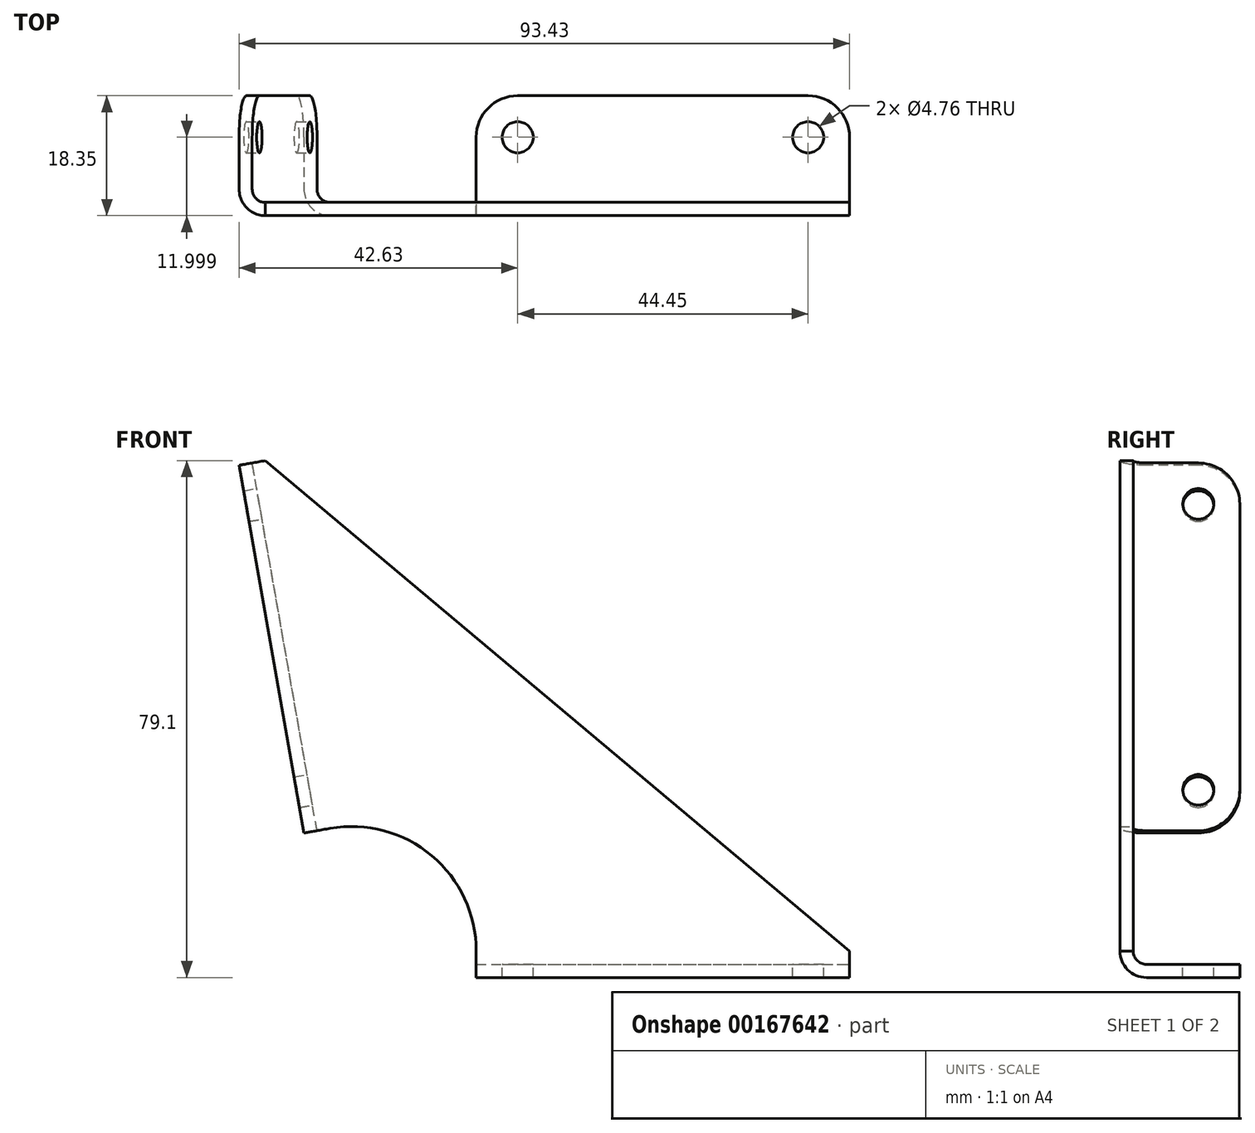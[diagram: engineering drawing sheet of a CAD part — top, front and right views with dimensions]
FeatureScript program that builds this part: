
annotation { "Feature Type Name" : "Feature", "Feature Type Description" : "" }
export const myFeature = defineFeature(function(context is Context, id is Id, definition is map)
    precondition{}
    {
        {
            var Q0;
            Q0=qCreatedBy(makeId("Front.planeOp"),FACE);
            var sketch = newSketch(context, id + "F0", { "sketchPlane" : qUnion([Q0])});
            skLineSegment(sketch, "E0", {"start": v(-3.3, 18.76) * mm, "end": v(-13.23, 75.04) * mm});
            skLineSegment(sketch, "E1", {"start": v(19.05, 0) * mm, "end": v(76.2, 0) * mm});
            skLineSegment(sketch, "E2", {"start": v(-13.23, 75.04) * mm, "end": v(76.2, 0) * mm});
            skArc(sketch, "E3", {"start": v(19.05, 0) * mm, "mid": v(12.25, 14.6) * mm, "end": v(-3.3, 18.76) * mm});
            skSolve(sketch);
        }
        {
            var Q0;
            Q0 = qSketchRegion(id + "F0", true);
            extrude(context, id + "F1", {"entities" : qUnion([Q0]), "depth" : 2.03 * mm});
        }
        {
            var Q0;
            Q0=makeQuery(id+"F1.opExtrude","SWEPT_FACE",FACE,{"disambiguationData":[OSD([sQuery(id+"F0.wireOp",EDGE,"E1")])]});
            var sketch = newSketch(context, id + "F2", { "sketchPlane" : qUnion([Q0])});
            skLineSegment(sketch, "E4", {"start": v(51.4, -2.03) * mm, "end": v(29.22, -2.03) * mm, "construction": true});
            skSolve(sketch);
        }
        {
            var Q0;
            {var subQ0=sQuery(id+"F0.wireOp",EDGE,"E1");Q0=makeQuery(id+"F2.imprint","IMPRINT",FACE,{"disambiguationData":[TD([[makeQuery(id+"F2.imprint","IMPRINT",EDGE,{"derivedFrom":makeQuery(id+"F1.opExtrude","CAP_EDGE",EDGE,{"disambiguationData":[OSD([subQ0])],"isStart":true})}),1.0]])]});}
            var Q1;
            Q1=sQuery(id+"F2.wireOp",EDGE,"E4");
            revolve(context, id + "F3", {"operationType" : NewBodyOperationType.ADD, "entities" : qUnion([Q0]), "axis" : qUnion([Q1]), "revolveType" : RevolveType.ONE_DIRECTION, "oppositeDirection" : true, "angle" : 90 * degree});
        }
        {
            var Q0;
            Q0=makeQuery(id+"F1.opExtrude","SWEPT_FACE",FACE,{"disambiguationData":[OSD([sQuery(id+"F0.wireOp",EDGE,"E0")])]});
            var sketch = newSketch(context, id + "F4", { "sketchPlane" : qUnion([Q0])});
            skLineSegment(sketch, "E5", {"start": v(-2.03, 20.89) * mm, "end": v(-2.03, 45.8) * mm, "construction": true});
            skSolve(sketch);
        }
        {
            var Q0;
            {var subQ0=sQuery(id+"F0.wireOp",EDGE,"E0");Q0=makeQuery(id+"F4.imprint","IMPRINT",FACE,{"disambiguationData":[TD([[makeQuery(id+"F4.imprint","IMPRINT",EDGE,{"derivedFrom":makeQuery(id+"F1.opExtrude","CAP_EDGE",EDGE,{"disambiguationData":[OSD([subQ0])],"isStart":true})}),-1.0]])]});}
            var Q1;
            Q1=sQuery(id+"F4.wireOp",EDGE,"E5");
            revolve(context, id + "F5", {"operationType" : NewBodyOperationType.ADD, "entities" : qUnion([Q0]), "axis" : qUnion([Q1]), "revolveType" : RevolveType.ONE_DIRECTION, "oppositeDirection" : true, "angle" : 90 * degree});
        }
        {
            var Q0;
            Q0=makeQuery(id+"F3.opRevolve","CAP_FACE",FACE,{"disambiguationData":[OSD([sQuery(id+"F0.wireOp",EDGE,"E1"),sQuery(id+"F0.wireOp",EDGE,"E2"),sQuery(id+"F0.wireOp",EDGE,"E3")])],"isStart":false});
            var Q1;
            Q1=makeQuery(id+"F5.opRevolve","CAP_FACE",FACE,{"disambiguationData":[OSD([sQuery(id+"F0.wireOp",EDGE,"E0"),sQuery(id+"F0.wireOp",EDGE,"E2"),sQuery(id+"F0.wireOp",EDGE,"E3")])],"isStart":false});
            extrude(context, id + "F6", {"entities" : qUnion([Q0, Q1]), "operationType" : NewBodyOperationType.ADD, "depth" : 14.29 * mm});
        }
        {
            var Q0;
            Q0=makeQuery(id+"F6.opExtrude","CAP_EDGE",EDGE,{"disambiguationData":[OSD([sQuery(id+"F0.wireOp",EDGE,"E0"),sQuery(id+"F0.wireOp",EDGE,"E2")])],"isStart":false});
            var Q1;
            Q1=makeQuery(id+"F6.opExtrude","CAP_EDGE",EDGE,{"disambiguationData":[OSD([sQuery(id+"F0.wireOp",EDGE,"E0"),sQuery(id+"F0.wireOp",EDGE,"E3")])],"isStart":false});
            var Q2;
            Q2=makeQuery(id+"F6.opExtrude","CAP_EDGE",EDGE,{"disambiguationData":[OSD([sQuery(id+"F0.wireOp",EDGE,"E1"),sQuery(id+"F0.wireOp",EDGE,"E3")])],"isStart":false});
            var Q3;
            Q3=makeQuery(id+"F6.opExtrude","CAP_EDGE",EDGE,{"disambiguationData":[OSD([sQuery(id+"F0.wireOp",EDGE,"E1"),sQuery(id+"F0.wireOp",EDGE,"E2")])],"isStart":false});
            fillet(context, id + "F7", {"entities" : qUnion([Q0, Q1, Q2, Q3]), "radius" : 6.35 * mm, "tangentPropagation" : true, "allowEdgeOverflow" : false});
        }
        {
            var Q0;
            {var subQ0=sQuery(id+"F0.wireOp",EDGE,"E0");Q0=makeQuery(id+"F6.opExtrude","SWEPT_FACE",FACE,{"disambiguationData":[OSD([subQ0]),TDD([makeQuery(id+"F5.opRevolve","CAP_EDGE",EDGE,{"disambiguationData":[OSD([subQ0]),TDD([makeQuery(id+"F4.imprint","IMPRINT",EDGE,{"derivedFrom":makeQuery(id+"F1.opExtrude","CAP_EDGE",EDGE,{"disambiguationData":[OSD([subQ0])],"isStart":true})})])],"isStart":false})])]});}
            var sketch = newSketch(context, id + "F8", { "sketchPlane" : qUnion([Q0])});
            skPoint(sketch, "E6", {"position": v(9.97, 69.85) * mm});
            skPoint(sketch, "E7", {"position": v(9.97, 25.4) * mm});
            skSolve(sketch);
        }
        {
            var Q0;
            {var subQ0=sQuery(id+"F0.wireOp",EDGE,"E1");Q0=makeQuery(id+"F6.opExtrude","SWEPT_FACE",FACE,{"disambiguationData":[OSD([subQ0]),TDD([makeQuery(id+"F3.opRevolve","CAP_EDGE",EDGE,{"disambiguationData":[OSD([subQ0]),TDD([makeQuery(id+"F2.imprint","IMPRINT",EDGE,{"derivedFrom":makeQuery(id+"F1.opExtrude","CAP_EDGE",EDGE,{"disambiguationData":[OSD([subQ0])],"isStart":true})})])],"isStart":false})])]});}
            var sketch = newSketch(context, id + "F9", { "sketchPlane" : qUnion([Q0])});
            skPoint(sketch, "E8", {"position": v(25.4, 9.97) * mm});
            skPoint(sketch, "E9", {"position": v(69.85, 9.97) * mm});
            skSolve(sketch);
        }
        {
            var Q0;
            Q0=sQuery(id+"F9.wireOp",VERTEX,"E8");
            var Q1;
            Q1=sQuery(id+"F9.wireOp",VERTEX,"E9");
            var Q2;
            Q2=sQuery(id+"F8.wireOp",VERTEX,"E7");
            var Q3;
            Q3=sQuery(id+"F8.wireOp",VERTEX,"E6");
            var Q4;
            Q4=makeQuery(id+"F1.opExtrude","SWEPT_BODY",BODY,{"disambiguationData":[OSD([sQuery(id+"F0.wireOp",EDGE,"E0"),sQuery(id+"F0.wireOp",EDGE,"E1"),sQuery(id+"F0.wireOp",EDGE,"E2"),sQuery(id+"F0.wireOp",EDGE,"E3")])]});
            hole(context, id + "F10", {"style" : HoleStyle.SIMPLE, "endStyle" : HoleEndStyle.THROUGH, "holeDiameter" : 4.76 * mm, "startFromSketch" : true, "locations" : qUnion([Q0, Q1, Q2, Q3]), "scope" : qUnion([Q4]), "isTappedThrough" : true});
        }
    });
